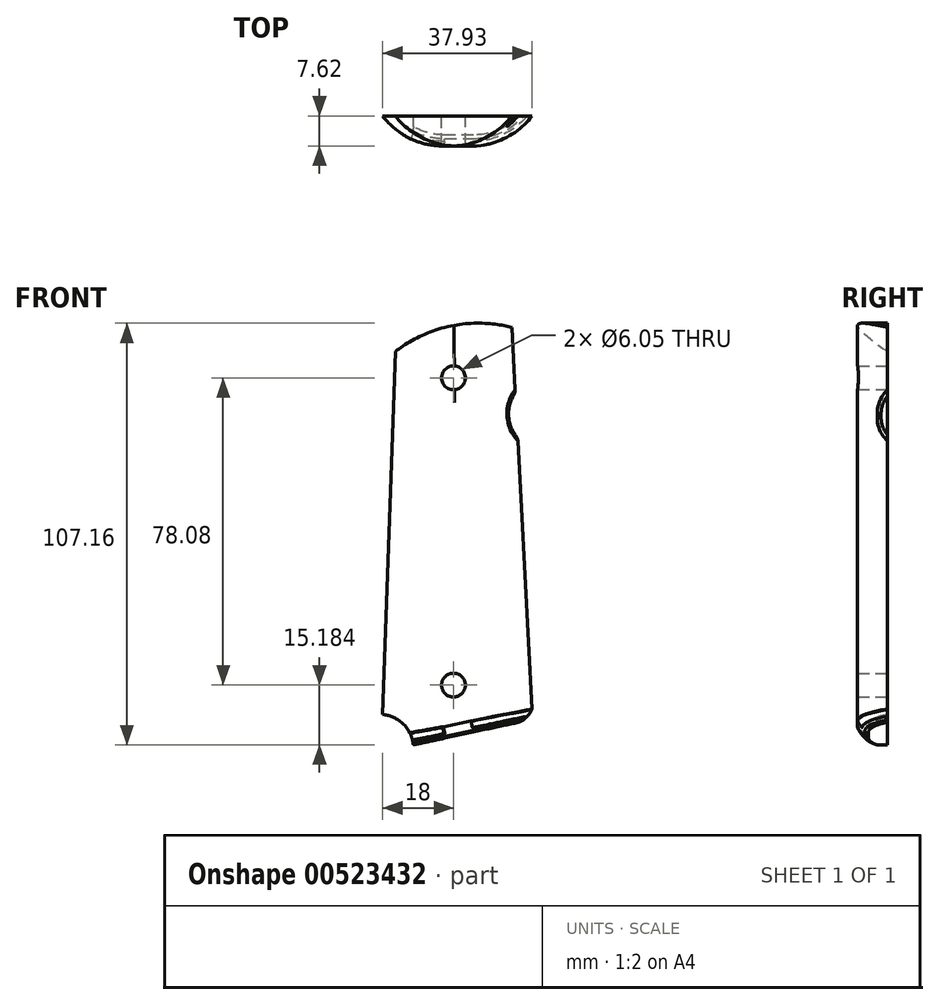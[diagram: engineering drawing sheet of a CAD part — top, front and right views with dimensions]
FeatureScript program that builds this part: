
annotation { "Feature Type Name" : "Feature", "Feature Type Description" : "" }
export const myFeature = defineFeature(function(context is Context, id is Id, definition is map)
    precondition{}
    {
        {
            var Q0;
            Q0=qCreatedBy(makeId("Front.planeOp"),FACE);
            var sketch = newSketch(context, id + "F0", { "sketchPlane" : qUnion([Q0])});
            skPoint(sketch, "E0.middle", {"position": v(0, 0) * mm});
            skLineSegment(sketch, "E1", {"start": v(0, 30.4) * mm, "end": v(0, -47.68) * mm, "construction": true});
            skLineSegment(sketch, "E2", {"start": v(-18.8, -47.71) * mm, "end": v(-18.8, -63.72) * mm, "construction": true});
            skLineSegment(sketch, "E3", {"start": v(0, 30.4) * mm, "end": v(23.11, 30.4) * mm, "construction": true});
            skLineSegment(sketch, "E4", {"start": v(23.11, 30.4) * mm, "end": v(23.11, 21.26) * mm, "construction": true});
            skArc(sketch, "E5", {"start": v(15.71, 26.63) * mm, "mid": v(13.98, 20.78) * mm, "end": v(16.32, 15.14) * mm});
            skArc(sketch, "E6", {"start": v(6.35, 44.54) * mm, "mid": v(14.57, 25.12) * mm, "end": v(-4.18, 15.48) * mm, "construction": true});
            skArc(sketch, "E7", {"start": v(-12.52, 38.69) * mm, "mid": v(-14.78, 27.8) * mm, "end": v(-8.92, 18.33) * mm, "construction": true});
            skArc(sketch, "E8", {"start": v(4.03, -28.51) * mm, "mid": v(17.76, -39.43) * mm, "end": v(17.24, -56.96) * mm, "construction": true});
            skArc(sketch, "E9", {"start": v(-4.87, -30.63) * mm, "mid": v(-14.16, -37.01) * mm, "end": v(-17.73, -47.71) * mm, "construction": true});
            skLineSegment(sketch, "E10", {"start": v(0, -47.68) * mm, "end": v(-18.8, -47.71) * mm, "construction": true});
            skLineSegment(sketch, "E11", {"start": v(0, 30.4) * mm, "end": v(0, 43.1) * mm, "construction": true});
            skLineSegment(sketch, "E12", {"start": v(0, 65.94) * mm, "end": v(6.35, 65.94) * mm, "construction": true});
            skPoint(sketch, "E12.startSnap0", {"position": v(0, 36.75) * mm});
            skLineSegment(sketch, "E13", {"start": v(6.35, 65.94) * mm, "end": v(6.35, -4.64) * mm, "construction": true});
            skArc(sketch, "E14", {"start": v(-14.79, 37.07) * mm, "mid": v(-0.68, 43.57) * mm, "end": v(14.84, 43.24) * mm});
            skLineSegment(sketch, "E15", {"start": v(14.84, 43.24) * mm, "end": v(15.71, 26.63) * mm, "construction": true});
            skLineSegment(sketch, "E16", {"start": v(-14.79, 37.07) * mm, "end": v(-18, -55.12) * mm});
            skLineSegment(sketch, "E17", {"start": v(14.84, 43.24) * mm, "end": v(15.71, 26.63) * mm});
            skPoint(sketch, "E18.endSnap0", {"position": v(-14.56, -56.16) * mm});
            skArc(sketch, "E19", {"start": v(-18.8, -55.08) * mm, "mid": v(-13, -57.31) * mm, "end": v(-10.2, -62.86) * mm});
            skPoint(sketch, "E20.orphan", {"position": v(-8, 43.1) * mm});
            skPoint(sketch, "E21.orphan", {"position": v(23.11, 30.4) * mm});
            skPoint(sketch, "E22", {"position": v(-15, 30.93) * mm});
            skLineSegment(sketch, "E23", {"start": v(-10.2, -62.86) * mm, "end": v(20.07, -56.36) * mm});
            skLineSegment(sketch, "E24.trimOffspring", {"start": v(16.32, 15.14) * mm, "end": v(20.07, -56.36) * mm, "construction": true});
            skLineSegment(sketch, "E25.trimOffspring", {"start": v(16.32, 15.14) * mm, "end": v(20.07, -56.36) * mm});
            skCircle(sketch, "E26", {"center": v(0, 30.4) * mm, "radius": 3.02 * mm});
            skCircle(sketch, "E27", {"center": v(0, -47.68) * mm, "radius": 3.02 * mm});
            skSolve(sketch);
        }
        {
            var Q0;
            Q0=makeQuery(id+"F0.imprint","IMPRINT",FACE,{"disambiguationData":[TD([[makeQuery(id+"F0.imprint","IMPRINT",EDGE,{"derivedFrom":sQuery(id+"F0.wireOp",EDGE,"E5")}),-1.0]])]});
            extrude(context, id + "F1", {"entities" : qUnion([Q0]), "depth" : 7.62 * mm, "offsetDistance" : 25.4 * mm});
        }
        {
            var Q0;
            Q0=makeQuery(id+"F1.opExtrude","CAP_EDGE",EDGE,{"disambiguationData":[OSD([sQuery(id+"F0.wireOp",EDGE,"E16")])],"isStart":false});
            var Q1;
            Q1=makeQuery(id+"F1.opExtrude","CAP_EDGE",EDGE,{"disambiguationData":[OSD([sQuery(id+"F0.wireOp",EDGE,"E25.trimOffspring")])],"isStart":false});
            fillet(context, id + "F2", {"entities" : qUnion([Q0, Q1]), "radius" : 19.62 * mm, "tangentPropagation" : true, "allowEdgeOverflow" : false});
        }
        {
            var Q0;
            Q0=makeQuery(id+"F2.opFillet","BLEND_EDGE",EDGE,{"blendedFrom":[makeQuery(id+"F1.opExtrude","CAP_EDGE",EDGE,{"disambiguationData":[OSD([sQuery(id+"F0.wireOp",EDGE,"E25.trimOffspring")])],"isStart":false}),makeQuery(id+"F1.opExtrude","SWEPT_FACE",FACE,{"disambiguationData":[OSD([sQuery(id+"F0.wireOp",EDGE,"E5")])]})],"blendedInto":[makeQuery(id+"F1.opExtrude","SWEPT_FACE",FACE,{"disambiguationData":[OSD([sQuery(id+"F0.wireOp",EDGE,"E5")])]})]});
            fillet(context, id + "F3", {"entities" : qUnion([Q0]), "radius" : 1.27 * mm, "tangentPropagation" : true, "allowEdgeOverflow" : false});
        }
        {
            var Q0;
            Q0=makeQuery(id+"F1.opExtrude","CAP_EDGE",EDGE,{"disambiguationData":[OSD([sQuery(id+"F0.wireOp",EDGE,"E23")])],"isStart":false});
            var Q1;
            Q1=makeQuery(id+"F2.opFillet","BLEND_EDGE",EDGE,{"blendedFrom":[makeQuery(id+"F1.opExtrude","CAP_EDGE",EDGE,{"disambiguationData":[OSD([sQuery(id+"F0.wireOp",EDGE,"E16")])],"isStart":false}),makeQuery(id+"F1.opExtrude","SWEPT_FACE",FACE,{"disambiguationData":[OSD([sQuery(id+"F0.wireOp",EDGE,"E23")])]})],"blendedInto":[makeQuery(id+"F1.opExtrude","SWEPT_FACE",FACE,{"disambiguationData":[OSD([sQuery(id+"F0.wireOp",EDGE,"E23")])]})]});
            var Q2;
            Q2=makeQuery(id+"F2.opFillet","BLEND_EDGE",EDGE,{"blendedFrom":[makeQuery(id+"F1.opExtrude","CAP_EDGE",EDGE,{"disambiguationData":[OSD([sQuery(id+"F0.wireOp",EDGE,"E25.trimOffspring")])],"isStart":false}),makeQuery(id+"F1.opExtrude","SWEPT_FACE",FACE,{"disambiguationData":[OSD([sQuery(id+"F0.wireOp",EDGE,"E23")])]})],"blendedInto":[makeQuery(id+"F1.opExtrude","SWEPT_FACE",FACE,{"disambiguationData":[OSD([sQuery(id+"F0.wireOp",EDGE,"E23")])]})]});
            chamfer(context, id + "F4", {"entities" : qUnion([Q0, Q1, Q2]), "width" : 2.3 * mm, "tangentPropagation" : true});
        }
        {
            var Q0;
            {var subQ0=makeQuery(id+"F1.opExtrude","SWEPT_FACE",FACE,{"disambiguationData":[OSD([sQuery(id+"F0.wireOp",EDGE,"E23")])]});Q0=makeQuery(id+"F4.opChamfer","BLEND_EDGE",EDGE,{"blendedFrom":[makeQuery(id+"F2.opFillet","BLEND_EDGE",EDGE,{"blendedFrom":[makeQuery(id+"F1.opExtrude","CAP_EDGE",EDGE,{"disambiguationData":[OSD([sQuery(id+"F0.wireOp",EDGE,"E16")])],"isStart":false}),subQ0],"blendedInto":[subQ0]}),subQ0],"blendedInto":[subQ0]});}
            var Q1;
            {var subQ0=sQuery(id+"F0.wireOp",EDGE,"E23");Q1=makeQuery(id+"F4.opChamfer","BLEND_EDGE",EDGE,{"blendedFrom":[makeQuery(id+"F1.opExtrude","CAP_EDGE",EDGE,{"disambiguationData":[OSD([subQ0])],"isStart":false}),makeQuery(id+"F1.opExtrude","SWEPT_FACE",FACE,{"disambiguationData":[OSD([subQ0])]})],"blendedInto":[makeQuery(id+"F1.opExtrude","SWEPT_FACE",FACE,{"disambiguationData":[OSD([subQ0])]})]});}
            var Q2;
            {var subQ0=makeQuery(id+"F1.opExtrude","SWEPT_FACE",FACE,{"disambiguationData":[OSD([sQuery(id+"F0.wireOp",EDGE,"E23")])]});Q2=makeQuery(id+"F4.opChamfer","BLEND_EDGE",EDGE,{"blendedFrom":[makeQuery(id+"F2.opFillet","BLEND_EDGE",EDGE,{"blendedFrom":[makeQuery(id+"F1.opExtrude","CAP_EDGE",EDGE,{"disambiguationData":[OSD([sQuery(id+"F0.wireOp",EDGE,"E25.trimOffspring")])],"isStart":false}),subQ0],"blendedInto":[subQ0]}),subQ0],"blendedInto":[subQ0]});}
            chamfer(context, id + "F5", {"entities" : qUnion([Q0, Q1, Q2]), "width" : 1.27 * mm, "tangentPropagation" : true});
        }
        {
            var Q0;
            {var subQ0=sQuery(id+"F0.wireOp",EDGE,"E25.trimOffspring");Q0=makeQuery(id+"F4.opChamfer","BLEND_EDGE",EDGE,{"blendedFrom":[makeQuery(id+"F2.opFillet","BLEND_EDGE",EDGE,{"blendedFrom":[makeQuery(id+"F1.opExtrude","CAP_EDGE",EDGE,{"disambiguationData":[OSD([subQ0])],"isStart":false}),makeQuery(id+"F1.opExtrude","SWEPT_FACE",FACE,{"disambiguationData":[OSD([sQuery(id+"F0.wireOp",EDGE,"E23")])]})],"blendedInto":[makeQuery(id+"F1.opExtrude","SWEPT_FACE",FACE,{"disambiguationData":[OSD([sQuery(id+"F0.wireOp",EDGE,"E23")])]})]}),makeQuery(id+"F2.opFillet","BLEND_FACE",FACE,{"disambiguationData":[OSD([subQ0])]})],"blendedInto":[makeQuery(id+"F2.opFillet","BLEND_FACE",FACE,{"disambiguationData":[OSD([subQ0])]})]});}
            var Q1;
            {var subQ0=sQuery(id+"F0.wireOp",EDGE,"E23");Q1=makeQuery(id+"F4.opChamfer","BLEND_EDGE",EDGE,{"blendedFrom":[makeQuery(id+"F1.opExtrude","CAP_EDGE",EDGE,{"disambiguationData":[OSD([subQ0])],"isStart":false}),makeQuery(id+"F1.opExtrude","CAP_FACE",FACE,{"disambiguationData":[OSD([sQuery(id+"F0.wireOp",EDGE,"E5"),sQuery(id+"F0.wireOp",EDGE,"E14"),sQuery(id+"F0.wireOp",EDGE,"E16"),sQuery(id+"F0.wireOp",EDGE,"E17"),sQuery(id+"F0.wireOp",EDGE,"E19"),subQ0,sQuery(id+"F0.wireOp",EDGE,"E25.trimOffspring"),sQuery(id+"F0.wireOp",EDGE,"E26"),sQuery(id+"F0.wireOp",EDGE,"E27")])],"isStart":false})],"blendedInto":[makeQuery(id+"F1.opExtrude","CAP_FACE",FACE,{"disambiguationData":[OSD([sQuery(id+"F0.wireOp",EDGE,"E5"),sQuery(id+"F0.wireOp",EDGE,"E14"),sQuery(id+"F0.wireOp",EDGE,"E16"),sQuery(id+"F0.wireOp",EDGE,"E17"),sQuery(id+"F0.wireOp",EDGE,"E19"),subQ0,sQuery(id+"F0.wireOp",EDGE,"E25.trimOffspring"),sQuery(id+"F0.wireOp",EDGE,"E26"),sQuery(id+"F0.wireOp",EDGE,"E27")])],"isStart":false})]});}
            var Q2;
            {var subQ0=sQuery(id+"F0.wireOp",EDGE,"E16");Q2=makeQuery(id+"F4.opChamfer","BLEND_EDGE",EDGE,{"blendedFrom":[makeQuery(id+"F2.opFillet","BLEND_EDGE",EDGE,{"blendedFrom":[makeQuery(id+"F1.opExtrude","CAP_EDGE",EDGE,{"disambiguationData":[OSD([subQ0])],"isStart":false}),makeQuery(id+"F1.opExtrude","SWEPT_FACE",FACE,{"disambiguationData":[OSD([sQuery(id+"F0.wireOp",EDGE,"E23")])]})],"blendedInto":[makeQuery(id+"F1.opExtrude","SWEPT_FACE",FACE,{"disambiguationData":[OSD([sQuery(id+"F0.wireOp",EDGE,"E23")])]})]}),makeQuery(id+"F2.opFillet","BLEND_FACE",FACE,{"disambiguationData":[OSD([subQ0])]})],"blendedInto":[makeQuery(id+"F2.opFillet","BLEND_FACE",FACE,{"disambiguationData":[OSD([subQ0])]})]});}
            chamfer(context, id + "F6", {"entities" : qUnion([Q0, Q1, Q2]), "width" : 1.52 * mm, "tangentPropagation" : true});
        }
        {
            var Q0;
            {var subQ0=sQuery(id+"F0.wireOp",EDGE,"E23");var subQ1=sQuery(id+"F0.wireOp",EDGE,"E16");Q0=makeQuery(id+"F6.opChamfer","BLEND_EDGE",EDGE,{"blendedFrom":[makeQuery(id+"F4.opChamfer","BLEND_EDGE",EDGE,{"blendedFrom":[makeQuery(id+"F2.opFillet","BLEND_EDGE",EDGE,{"blendedFrom":[makeQuery(id+"F1.opExtrude","CAP_EDGE",EDGE,{"disambiguationData":[OSD([subQ1])],"isStart":false}),makeQuery(id+"F1.opExtrude","SWEPT_FACE",FACE,{"disambiguationData":[OSD([subQ0])]})],"blendedInto":[makeQuery(id+"F1.opExtrude","SWEPT_FACE",FACE,{"disambiguationData":[OSD([subQ0])]})]}),makeQuery(id+"F2.opFillet","BLEND_FACE",FACE,{"disambiguationData":[OSD([subQ1])]})],"blendedInto":[makeQuery(id+"F2.opFillet","BLEND_FACE",FACE,{"disambiguationData":[OSD([subQ1])]})]}),makeQuery(id+"F4.opChamfer","BLEND_FACE",FACE,{"disambiguationData":[OSD([subQ1,subQ0])]})],"blendedInto":[makeQuery(id+"F4.opChamfer","BLEND_FACE",FACE,{"disambiguationData":[OSD([subQ1,subQ0])]})]});}
            var Q1;
            {var subQ0=sQuery(id+"F0.wireOp",EDGE,"E25.trimOffspring");var subQ1=sQuery(id+"F0.wireOp",EDGE,"E23");Q1=makeQuery(id+"F6.opChamfer","BLEND_EDGE",EDGE,{"disambiguationData":[OD(1.0)],"blendedFrom":[makeQuery(id+"F4.opChamfer","BLEND_EDGE",EDGE,{"blendedFrom":[makeQuery(id+"F2.opFillet","BLEND_EDGE",EDGE,{"blendedFrom":[makeQuery(id+"F1.opExtrude","CAP_EDGE",EDGE,{"disambiguationData":[OSD([subQ0])],"isStart":false}),makeQuery(id+"F1.opExtrude","SWEPT_FACE",FACE,{"disambiguationData":[OSD([subQ1])]})],"blendedInto":[makeQuery(id+"F1.opExtrude","SWEPT_FACE",FACE,{"disambiguationData":[OSD([subQ1])]})]}),makeQuery(id+"F2.opFillet","BLEND_FACE",FACE,{"disambiguationData":[OSD([subQ0])]})],"blendedInto":[makeQuery(id+"F2.opFillet","BLEND_FACE",FACE,{"disambiguationData":[OSD([subQ0])]})]}),makeQuery(id+"F4.opChamfer","BLEND_FACE",FACE,{"disambiguationData":[OSD([subQ1,subQ0])]})],"blendedInto":[makeQuery(id+"F4.opChamfer","BLEND_FACE",FACE,{"disambiguationData":[OSD([subQ1,subQ0])]})]});}
            var Q2;
            {var subQ0=sQuery(id+"F0.wireOp",EDGE,"E23");Q2=makeQuery(id+"F6.opChamfer","BLEND_EDGE",EDGE,{"disambiguationData":[OD(1.0)],"blendedFrom":[makeQuery(id+"F4.opChamfer","BLEND_EDGE",EDGE,{"blendedFrom":[makeQuery(id+"F1.opExtrude","CAP_EDGE",EDGE,{"disambiguationData":[OSD([subQ0])],"isStart":false}),makeQuery(id+"F1.opExtrude","CAP_FACE",FACE,{"disambiguationData":[OSD([sQuery(id+"F0.wireOp",EDGE,"E5"),sQuery(id+"F0.wireOp",EDGE,"E14"),sQuery(id+"F0.wireOp",EDGE,"E16"),sQuery(id+"F0.wireOp",EDGE,"E17"),sQuery(id+"F0.wireOp",EDGE,"E19"),subQ0,sQuery(id+"F0.wireOp",EDGE,"E25.trimOffspring"),sQuery(id+"F0.wireOp",EDGE,"E26"),sQuery(id+"F0.wireOp",EDGE,"E27")])],"isStart":false})],"blendedInto":[makeQuery(id+"F1.opExtrude","CAP_FACE",FACE,{"disambiguationData":[OSD([sQuery(id+"F0.wireOp",EDGE,"E5"),sQuery(id+"F0.wireOp",EDGE,"E14"),sQuery(id+"F0.wireOp",EDGE,"E16"),sQuery(id+"F0.wireOp",EDGE,"E17"),sQuery(id+"F0.wireOp",EDGE,"E19"),subQ0,sQuery(id+"F0.wireOp",EDGE,"E25.trimOffspring"),sQuery(id+"F0.wireOp",EDGE,"E26"),sQuery(id+"F0.wireOp",EDGE,"E27")])],"isStart":false})]}),makeQuery(id+"F4.opChamfer","BLEND_FACE",FACE,{"disambiguationData":[OSD([subQ0])]})],"blendedInto":[makeQuery(id+"F4.opChamfer","BLEND_FACE",FACE,{"disambiguationData":[OSD([subQ0])]})]});}
            fillet(context, id + "F7", {"entities" : qUnion([Q0, Q1, Q2]), "radius" : 5.08 * mm, "tangentPropagation" : true, "allowEdgeOverflow" : false});
        }
    });
